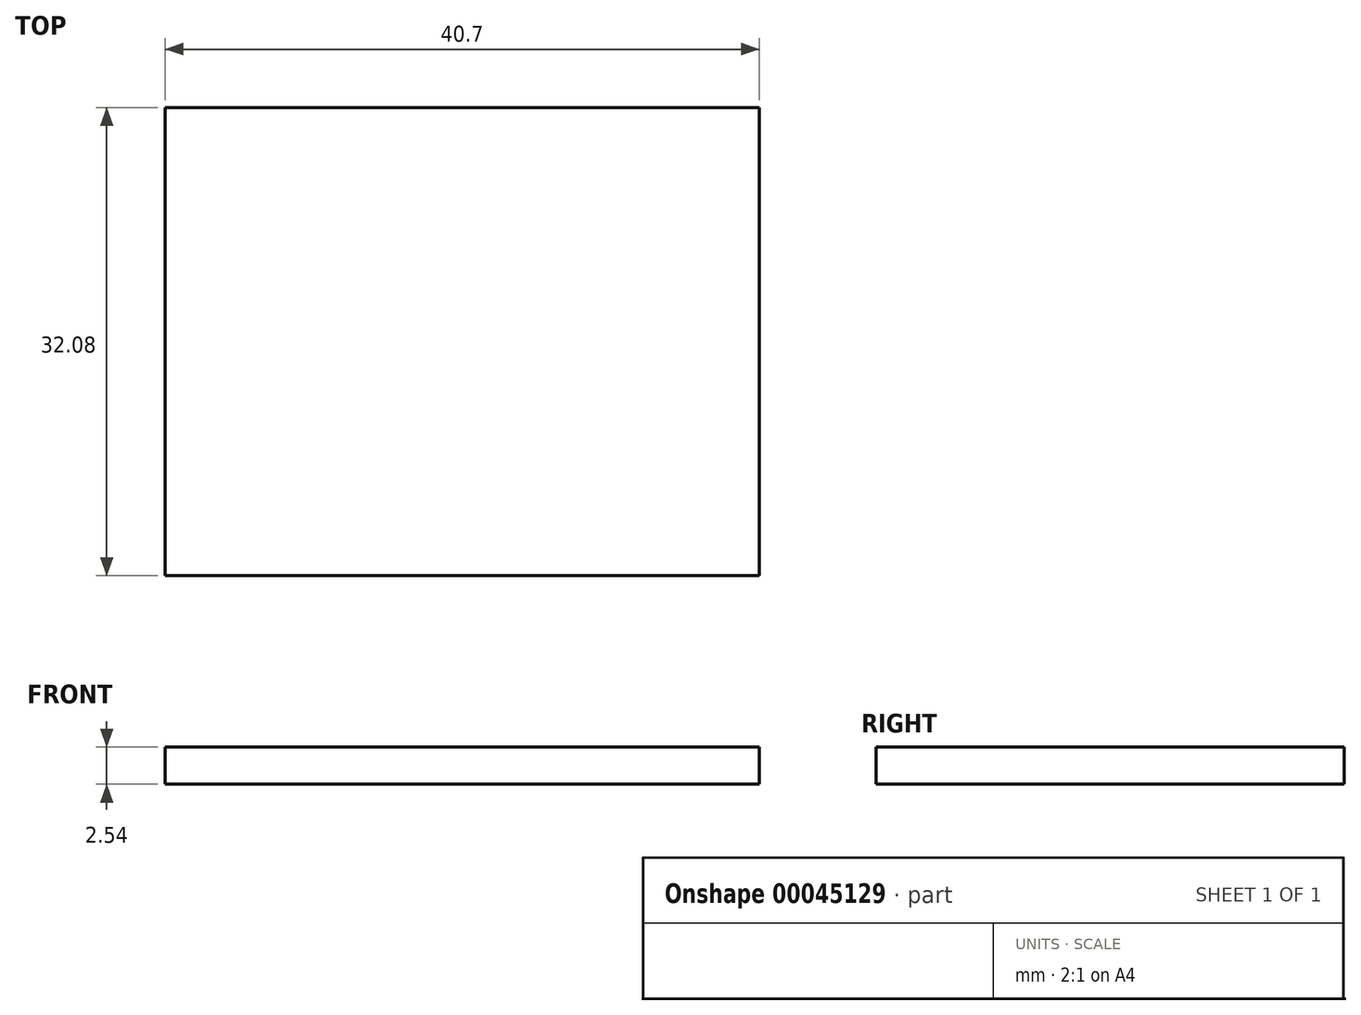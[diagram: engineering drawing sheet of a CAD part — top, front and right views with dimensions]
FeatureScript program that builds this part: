
annotation { "Feature Type Name" : "Feature", "Feature Type Description" : "" }
export const myFeature = defineFeature(function(context is Context, id is Id, definition is map)
    precondition{}
    {
        {
            var Q0;
            Q0=qCreatedBy(makeId("Top.planeOp"),FACE);
            var sketch = newSketch(context, id + "F0", { "sketchPlane" : qUnion([Q0])});
            skLineSegment(sketch, "E0.rect.bottom", {"start": v(20.35, 16.04) * mm, "end": v(-20.35, 16.04) * mm});
            skLineSegment(sketch, "E0.rect.top", {"start": v(20.35, -16.04) * mm, "end": v(-20.35, -16.04) * mm});
            skLineSegment(sketch, "E0.rect.left", {"start": v(20.35, 16.04) * mm, "end": v(20.35, -16.04) * mm});
            skLineSegment(sketch, "E0.rect.right", {"start": v(-20.35, 16.04) * mm, "end": v(-20.35, -16.04) * mm});
            skPoint(sketch, "E0.rect.middle", {"position": v(0, 0) * mm});
            skSolve(sketch);
        }
        {
            var Q0;
            Q0 = qSketchRegion(id + "F0", true);
            extrude(context, id + "F1", {"entities" : qUnion([Q0]), "depth" : 2.54 * mm});
        }
    });
